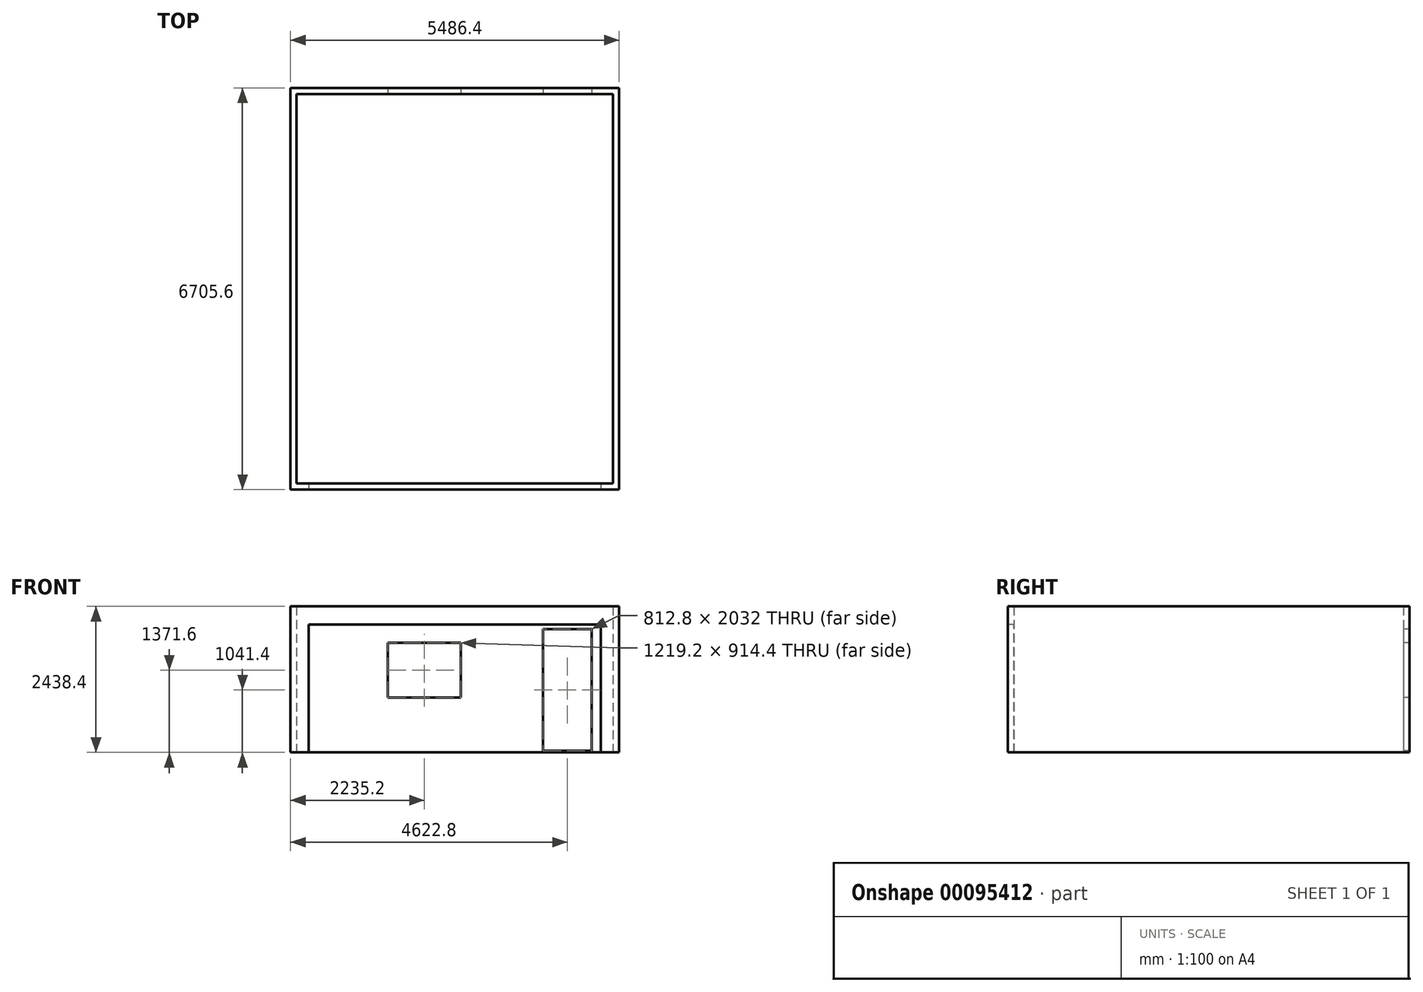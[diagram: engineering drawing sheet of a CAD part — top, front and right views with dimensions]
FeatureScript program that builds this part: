
annotation { "Feature Type Name" : "Feature", "Feature Type Description" : "" }
export const myFeature = defineFeature(function(context is Context, id is Id, definition is map)
    precondition{}
    {
        {
            var Q0;
            Q0=qCreatedBy(makeId("Top.planeOp"),FACE);
            var sketch = newSketch(context, id + "F0", { "sketchPlane" : qUnion([Q0])});
            skLineSegment(sketch, "E0.bottom", {"start": v(2743.2, 3352.8) * mm, "end": v(-2743.2, 3352.8) * mm});
            skLineSegment(sketch, "E0.top", {"start": v(2743.2, -3352.8) * mm, "end": v(-2743.2, -3352.8) * mm});
            skLineSegment(sketch, "E0.left", {"start": v(2743.2, 3352.8) * mm, "end": v(2743.2, -3352.8) * mm});
            skLineSegment(sketch, "E0.right", {"start": v(-2743.2, 3352.8) * mm, "end": v(-2743.2, -3352.8) * mm});
            skPoint(sketch, "E0.middle", {"position": v(0, 0) * mm});
            skLineSegment(sketch, "E1.bottom", {"start": v(2641.6, 3251.2) * mm, "end": v(-2641.6, 3251.2) * mm});
            skLineSegment(sketch, "E1.top", {"start": v(2641.6, -3251.2) * mm, "end": v(-2641.6, -3251.2) * mm});
            skLineSegment(sketch, "E1.left", {"start": v(2641.6, 3251.2) * mm, "end": v(2641.6, -3251.2) * mm});
            skLineSegment(sketch, "E1.right", {"start": v(-2641.6, 3251.2) * mm, "end": v(-2641.6, -3251.2) * mm});
            skSolve(sketch);
        }
        {
            var Q0;
            Q0 = qSketchRegion(id + "F0", true);
            extrude(context, id + "F1", {"entities" : qUnion([Q0]), "depth" : 2438.4 * mm});
        }
        {
            var Q0;
            Q0=makeQuery(id+"F1.opExtrude","SWEPT_FACE",FACE,{"disambiguationData":[OSD([sQuery(id+"F0.wireOp",EDGE,"E1.bottom")])]});
            var sketch = newSketch(context, id + "F2", { "sketchPlane" : qUnion([Q0])});
            skLineSegment(sketch, "E2.bottom", {"start": v(101.6, 1828.8) * mm, "end": v(-1117.6, 1828.8) * mm});
            skLineSegment(sketch, "E2.top", {"start": v(101.6, 914.4) * mm, "end": v(-1117.6, 914.4) * mm});
            skLineSegment(sketch, "E2.left", {"start": v(101.6, 1828.8) * mm, "end": v(101.6, 914.4) * mm});
            skLineSegment(sketch, "E2.right", {"start": v(-1117.6, 1828.8) * mm, "end": v(-1117.6, 914.4) * mm});
            skPoint(sketch, "E2.middle", {"position": v(-508, 1371.6) * mm});
            skSolve(sketch);
        }
        {
            var Q0;
            Q0 = qSketchRegion(id + "F2", true);
            extrude(context, id + "F3", {"entities" : qUnion([Q0]), "operationType" : NewBodyOperationType.REMOVE, "endBound" : BoundingType.UP_TO_NEXT, "oppositeDirection" : true, "depth" : 25.4 * mm});
        }
        {
            var Q0;
            Q0=makeQuery(id+"F1.opExtrude","SWEPT_FACE",FACE,{"disambiguationData":[OSD([sQuery(id+"F0.wireOp",EDGE,"E1.bottom")])]});
            var sketch = newSketch(context, id + "F4", { "sketchPlane" : qUnion([Q0])});
            skLineSegment(sketch, "E3.bottom", {"start": v(1473.2, 2057.4) * mm, "end": v(2286, 2057.4) * mm});
            skLineSegment(sketch, "E3.top", {"start": v(1473.2, 25.4) * mm, "end": v(2286, 25.4) * mm});
            skLineSegment(sketch, "E3.left", {"start": v(1473.2, 2057.4) * mm, "end": v(1473.2, 25.4) * mm});
            skLineSegment(sketch, "E3.right", {"start": v(2286, 2057.4) * mm, "end": v(2286, 25.4) * mm});
            skPoint(sketch, "E3.middle", {"position": v(1879.6, 1041.4) * mm});
            skSolve(sketch);
        }
        {
            var Q0;
            Q0 = qSketchRegion(id + "F4", true);
            extrude(context, id + "F5", {"entities" : qUnion([Q0]), "operationType" : NewBodyOperationType.REMOVE, "endBound" : BoundingType.UP_TO_NEXT, "oppositeDirection" : true, "depth" : 25.4 * mm});
        }
        {
            var Q0;
            Q0=makeQuery(id+"F1.opExtrude","SWEPT_FACE",FACE,{"disambiguationData":[OSD([sQuery(id+"F0.wireOp",EDGE,"E0.top")])]});
            var sketch = newSketch(context, id + "F6", { "sketchPlane" : qUnion([Q0])});
            skLineSegment(sketch, "E4.bottom", {"start": v(2438.4, 2133.6) * mm, "end": v(-2438.4, 2133.6) * mm});
            skLineSegment(sketch, "E4.top", {"start": v(2438.4, 0) * mm, "end": v(-2438.4, 0) * mm});
            skLineSegment(sketch, "E4.left", {"start": v(2438.4, 2133.6) * mm, "end": v(2438.4, 0) * mm});
            skLineSegment(sketch, "E4.right", {"start": v(-2438.4, 2133.6) * mm, "end": v(-2438.4, 0) * mm});
            skPoint(sketch, "E4.middle", {"position": v(0, 1066.8) * mm});
            skLineSegment(sketch, "E5", {"start": v(0, 1066.8) * mm, "end": v(0, 0) * mm, "construction": true});
            skSolve(sketch);
        }
        {
            var Q0;
            Q0=makeQuery(id+"F6.imprint","IMPRINT",FACE,{"disambiguationData":[TD([[makeQuery(id+"F6.imprint","IMPRINT",EDGE,{"derivedFrom":sQuery(id+"F6.wireOp",EDGE,"E4.bottom")}),1.0]])]});
            extrude(context, id + "F7", {"entities" : qUnion([Q0]), "operationType" : NewBodyOperationType.REMOVE, "endBound" : BoundingType.UP_TO_NEXT, "oppositeDirection" : true, "depth" : 25.4 * mm});
        }
    });
